# Revit family: 110104-00041 Колодец кабельный полимерный ККП-1-ССД
name_source: partatom
category: Обобщенные модели
units: mm (PartAtom-declared; Revit-internal decimal feet)

## family parameters
Всегда вертикально = Да
Может служить основой для арматурных стержней = Нет
На основе рабочей плоскости = Нет
Общий = Нет
При загрузке вырезать с полостями = Нет
Размер круглого соединителя = Использовать диаметр
Тип детали = Нормальный
Точка расчета площади = Нет

## types (1)
- Колодец кабельный полимерный ККП-1-ССД
    ADSK_Высота, без крышки мм = 450 мм
    ADSK_Высота, мм = 500 мм
    ADSK_Диаметр корпуса, мм = 600 мм
    ADSK_Диаметр крышки = 490 мм
    ADSK_Изготовитель = АО "СВЯЗЬСТРОЙДЕТАЛЬ"
    ADSK_Код изделия = 110104-00041
    ADSK_Кол-во и размер площадок для ввода трубы, шт/мм. = 8/200х320
    ADSK_Марка = Колодцы кабельные пластиковые
    ADSK_Масса = 9
    ADSK_Материал = Полиэтилен низкого давления
    ADSK_Наименование = Колодец кабельный полимерный ККП-1-ССД
    ADSK_Ссылка на сайт = https://www.ssd.ru
    Отметка по умолчанию = 0 мм
